# Revit family: NLRS_57_DUA_UN_Jaloezieklep_LT_KxVTEx_Solid_Air
name_source: partatom
category: Duct Accessories
units: mm (PartAtom-declared; Revit-internal decimal feet)

## family parameters
Always vertical = Yes
Cut with Voids When Loaded = No
OmniClass Number = 23.75.70.14.34
OmniClass Title = Air Duct Accessories
Part Type = Breaks Into
Round Connector Dimension = Use Diameter
Shared = No
Work Plane-Based = No

## types (6) — shared parameters
Assembly Code = 57.00
Manufacturer = Solid Air Climate Solutions
NLRS_C_content_datum_uitgifte = 01-05-2023
NLRS_C_content_provider = Solid Air Climate Solutions
NLRS_C_content_versie = 3.20.00
SACS_Data_Hidden = K_VTEx
URL = https://solid-air.nl
zero-valued in all types: Default Elevation

## per-type parameters (varying)
| type | Description | SACS_Max_Width | SACS_Option_1 | SACS_Option_1_Value | SACS_Option_2 | SACS_Option_2_Value | Type Comments |
| KIVTEH | Volume damper suitable for manual operation | 1300 mm  [stored 4.26509 ft] | Standard (I) | 0 | Manual operation (H) | 0 | Maximum size: 1300x1200 |
| KIVTEG | Volume damper suitable for motorized operation | 1300 mm  [stored 4.26509 ft] | Standard (I) | 0 | Suitable for motorized operation (G) | 1 | Maximum size: 1300x1200 |
| KRVTEH | Volume damper suitable for manual operation | 1200 mm  [stored 3.93701 ft] | Rubber seal on air-blades (R) | 1 | Manual operation (H) | 0 | Maximum size: 1200x1200 |
| KRVTEG | Volume damper suitable for motorized operation | 1200 mm  [stored 3.93701 ft] | Rubber seal on air-blades (R) | 1 | Suitable for motorized operation (G) | 1 | Maximum size: 1200x1200 |
| KLVTEH | Volume damper suitable for manual operation | 1200 mm  [stored 3.93701 ft] | Air-tight class 4 according EN 1751 (L) | 2 | Manual operation (H) | 0 | Maximum size: 1200x1200 |
| KLVTEG | Volume damper suitable for motorized operation | 1200 mm  [stored 3.93701 ft] | Air-tight class 4 according EN 1751 (L) | 2 | Suitable for motorized operation (G) | 1 | Maximum size: 1200x1200 |

note: column(s) folded — value = type name in every type: Model

note: [stored X ft] marks values corroborated as IEEE doubles in the binary element streams (Revit-internal decimal feet)

## geometry (parser evidence)
native form markers: Sweep x6
no freeform markers — native parametric forms only
